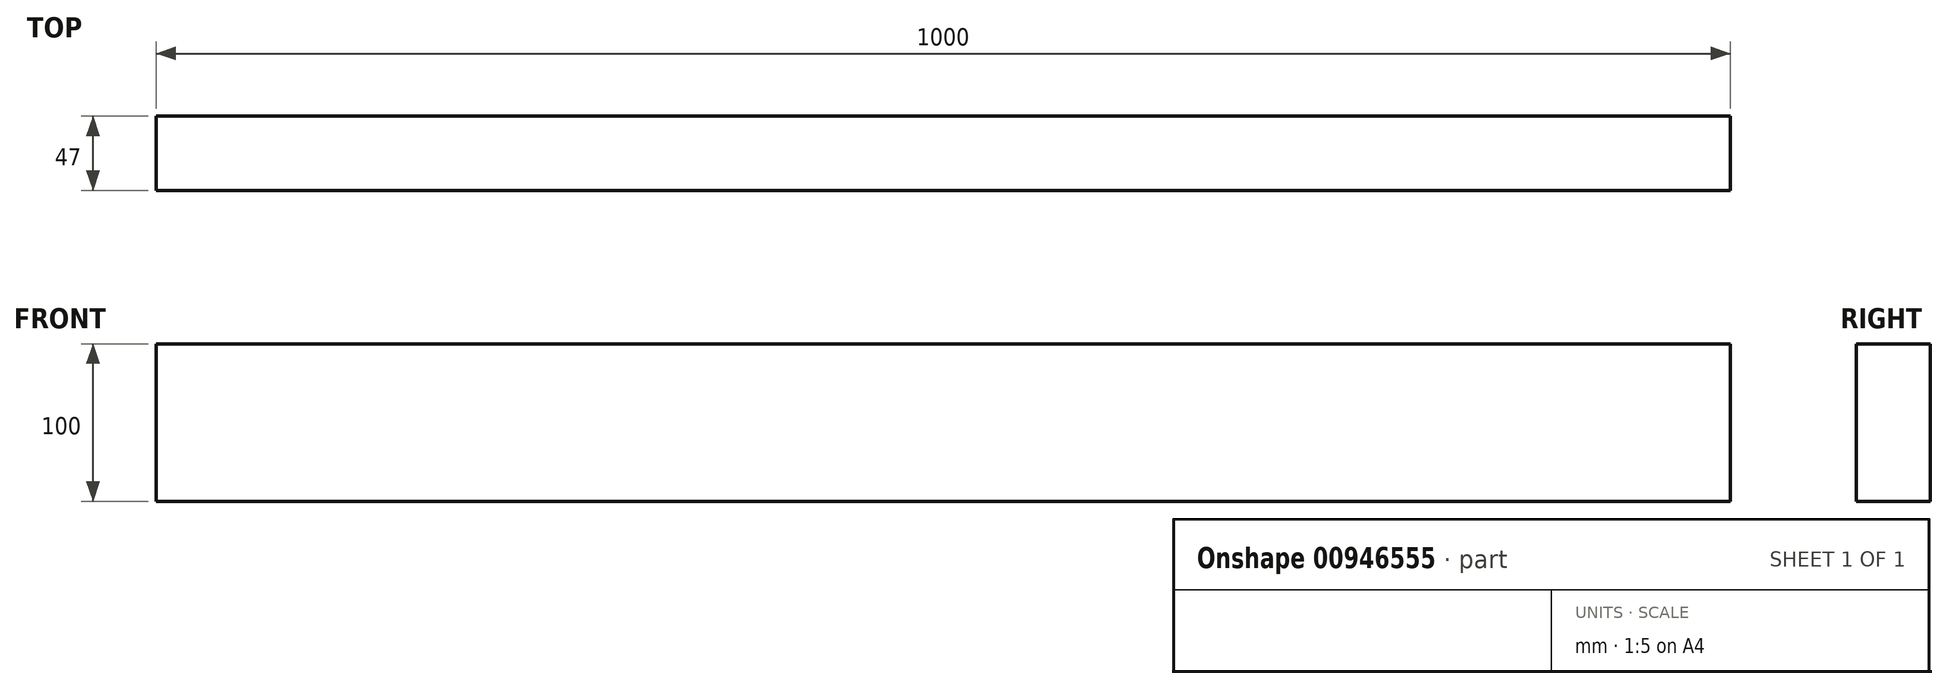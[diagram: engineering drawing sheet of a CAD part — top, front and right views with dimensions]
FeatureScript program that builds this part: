
annotation { "Feature Type Name" : "Feature", "Feature Type Description" : "" }
export const myFeature = defineFeature(function(context is Context, id is Id, definition is map)
    precondition{}
    {
        {
            var Q0;
            Q0=qCreatedBy(makeId("Right.planeOp"),FACE);
            var sketch = newSketch(context, id + "F0", { "sketchPlane" : qUnion([Q0])});
            skLineSegment(sketch, "E0.bottom", {"start": v(0, 0) * mm, "end": v(-47, 0) * mm});
            skLineSegment(sketch, "E0.top", {"start": v(0, 100) * mm, "end": v(-47, 100) * mm});
            skLineSegment(sketch, "E0.left", {"start": v(0, 0) * mm, "end": v(0, 100) * mm});
            skLineSegment(sketch, "E0.right", {"start": v(-47, 0) * mm, "end": v(-47, 100) * mm});
            skSolve(sketch);
        }
        {
            var Q0;
            Q0=qSketchRegion(id+"F0",true);
            extrude(context, id + "F1", {"entities" : qUnion([Q0]), "depth" : 1000 * mm, "offsetDistance" : 25 * mm});
        }
    });
